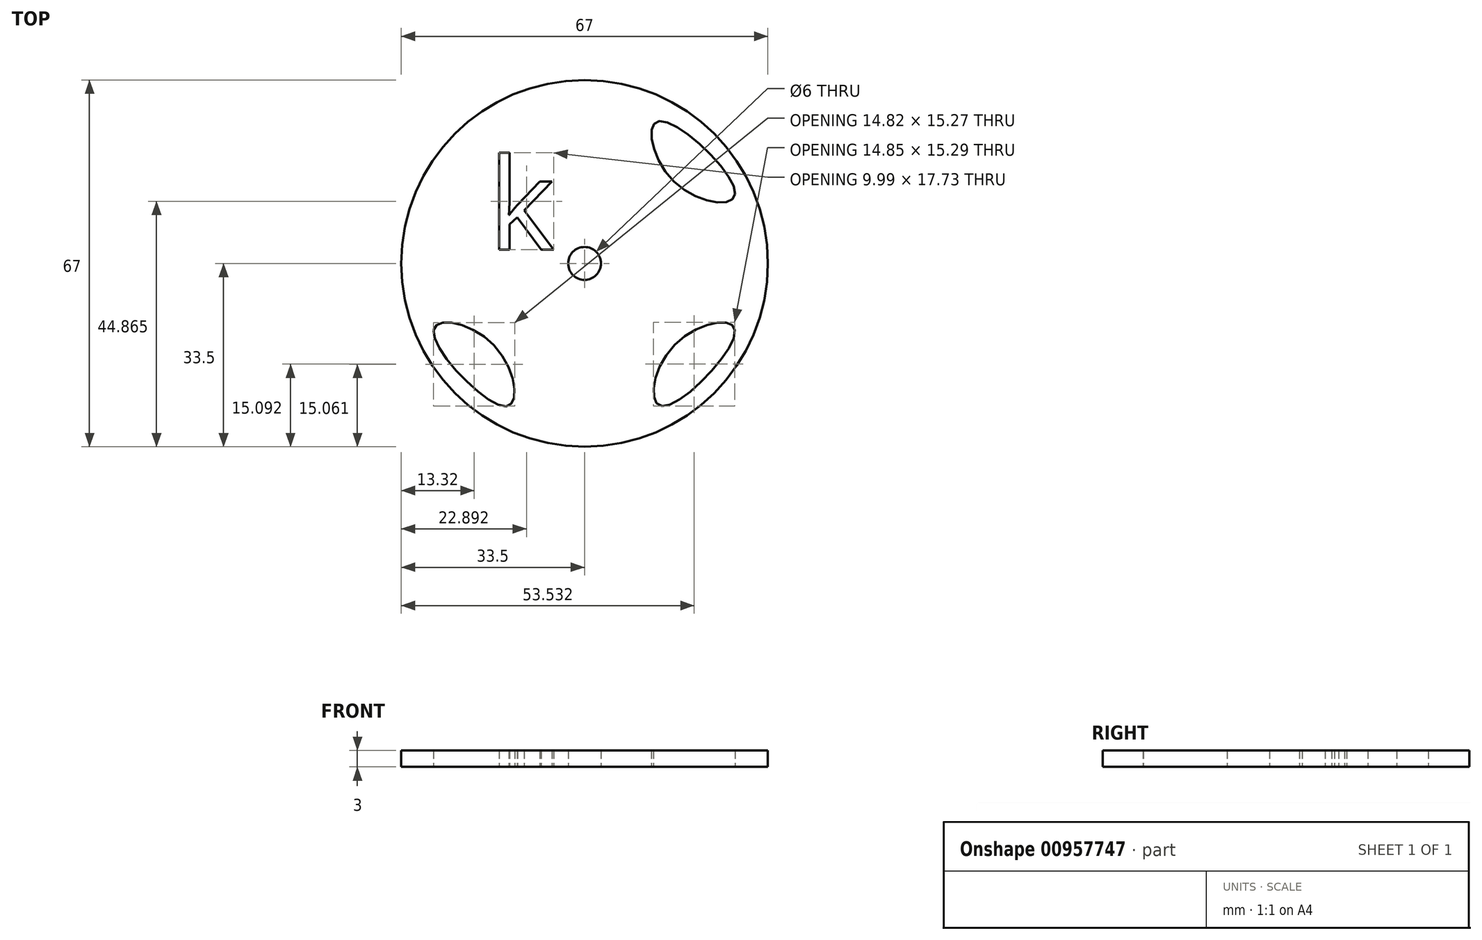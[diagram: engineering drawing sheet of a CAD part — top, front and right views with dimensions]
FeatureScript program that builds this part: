
annotation { "Feature Type Name" : "Feature", "Feature Type Description" : "" }
export const myFeature = defineFeature(function(context is Context, id is Id, definition is map)
    precondition{}
    {
        {
            var Q0;
            Q0=qCreatedBy(makeId("Top.planeOp"),FACE);
            var sketch = newSketch(context, id + "F0", { "sketchPlane" : qUnion([Q0])});
            skCircle(sketch, "E0", {"center": v(0, 0) * mm, "radius": 33.5 * mm});
            skCircle(sketch, "E1", {"center": v(0, 0) * mm, "radius": 3 * mm});
            skText(sketch, "E2", { "text": "k", "fontName": "OpenSans-Regular.ttf"});
            skFitSpline(sketch, "E3", {"points": [v(14.15, -26.05) * mm, v(27.46, -12.17) * mm, v(16.32, -15.03) * mm, v(14.15, -26.05) * mm]});
            skFitSpline(sketch, "E4", {"points": [v(-27.59, -12.22) * mm, v(-14.27, -26.1) * mm, v(-16.67, -14.85) * mm, v(-27.59, -12.22) * mm]});
            skFitSpline(sketch, "E5", {"points": [v(27.5, 12.69) * mm, v(13.62, 26) * mm, v(16.48, 14.86) * mm, v(27.5, 12.69) * mm]});
            const initialGuessF0  = {"E2": [-0.01761, 0.0025, 1, 0, 0.0168]};
            skSetInitialGuess(sketch, initialGuessF0);
            skSolve(sketch);
        }
        {
            var Q0;
            Q0 = qSketchRegion(id + "F0", true);
            extrude(context, id + "F1", {"entities" : qUnion([Q0]), "depth" : 3 * mm, "offsetDistance" : 25 * mm});
        }
    });
